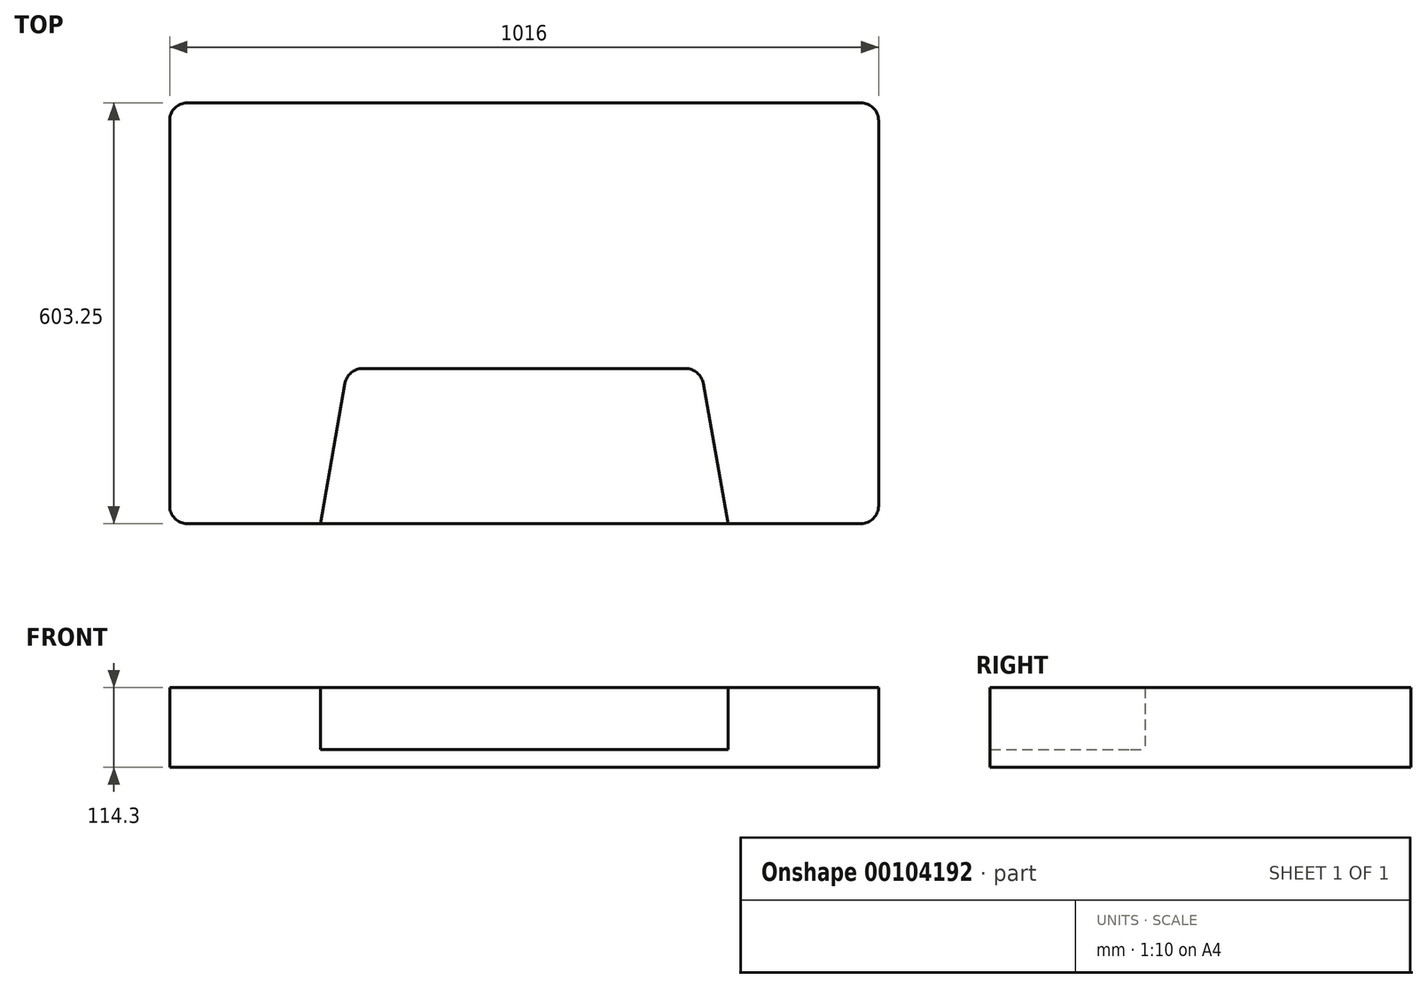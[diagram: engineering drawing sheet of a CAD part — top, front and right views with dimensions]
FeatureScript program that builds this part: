
annotation { "Feature Type Name" : "Feature", "Feature Type Description" : "" }
export const myFeature = defineFeature(function(context is Context, id is Id, definition is map)
    precondition{}
    {
        {
            var Q0;
            Q0=qCreatedBy(makeId("Top.planeOp"),FACE);
            var sketch = newSketch(context, id + "F0", { "sketchPlane" : qUnion([Q0])});
            skLineSegment(sketch, "E0.bottom", {"start": v(-508, 0) * mm, "end": v(508, 0) * mm});
            skLineSegment(sketch, "E0.top", {"start": v(-508, -603.25) * mm, "end": v(508, -603.25) * mm});
            skLineSegment(sketch, "E0.left", {"start": v(-508, 0) * mm, "end": v(-508, -603.25) * mm});
            skLineSegment(sketch, "E0.right", {"start": v(508, 0) * mm, "end": v(508, -603.25) * mm});
            skLineSegment(sketch, "E1", {"start": v(-292.1, -603.25) * mm, "end": v(-252.91, -381) * mm});
            skLineSegment(sketch, "E2", {"start": v(-252.91, -381) * mm, "end": v(252.91, -381) * mm});
            skLineSegment(sketch, "E3", {"start": v(252.91, -381) * mm, "end": v(292.1, -603.25) * mm});
            skLineSegment(sketch, "E4", {"start": v(0, 0) * mm, "end": v(0, -381) * mm, "construction": true});
            skSolve(sketch);
        }
        {
            var Q0;
            Q0=qSketchRegion(id+"F0",true);
            extrude(context, id + "F1", {"entities" : qUnion([Q0]), "depth" : 114.3 * mm});
        }
        {
            var Q0;
            {var subQ1=sQuery(id+"F0.wireOp",EDGE,"E1");Q0=makeQuery(id+"F0.imprint","IMPRINT",FACE,{"disambiguationData":[TD([[makeQuery(id+"F0.imprint","IMPRINT",EDGE,{"derivedFrom":subQ1}),-1.0]])]});}
            extrude(context, id + "F2", {"entities" : qUnion([Q0]), "operationType" : NewBodyOperationType.REMOVE, "endBound" : BoundingType.THROUGH_ALL, "depth" : 50.8 * mm, "hasSecondDirection" : true, "secondDirectionOppositeDirection" : false, "secondDirectionDepth" : 25.4 * mm});
        }
        {
            var Q0;
            Q0=makeQuery(id+"F1.opExtrude","SWEPT_EDGE",EDGE,{"disambiguationData":[OSD([sQuery(id+"F0.wireOp",EDGE,"E0.top"),sQuery(id+"F0.wireOp",EDGE,"E0.left")])]});
            var Q1;
            Q1=makeQuery(id+"F1.opExtrude","SWEPT_EDGE",EDGE,{"disambiguationData":[OSD([sQuery(id+"F0.wireOp",EDGE,"E0.top"),sQuery(id+"F0.wireOp",EDGE,"E0.right")])]});
            var Q2;
            Q2=makeQuery(id+"F2.boolean.opBoolean","COPY",EDGE,{"derivedFrom":makeQuery(id+"F2.opExtrude","SWEPT_EDGE",EDGE,{"disambiguationData":[OSD([sQuery(id+"F0.wireOp",EDGE,"E0.top"),sQuery(id+"F0.wireOp",EDGE,"E1")])]})});
            var Q3;
            Q3=makeQuery(id+"F2.boolean.opBoolean","COPY",EDGE,{"derivedFrom":makeQuery(id+"F2.opExtrude","SWEPT_EDGE",EDGE,{"disambiguationData":[OSD([sQuery(id+"F0.wireOp",EDGE,"E1"),sQuery(id+"F0.wireOp",EDGE,"E2")])]})});
            var Q4;
            Q4=makeQuery(id+"F2.boolean.opBoolean","COPY",EDGE,{"derivedFrom":makeQuery(id+"F2.opExtrude","SWEPT_EDGE",EDGE,{"disambiguationData":[OSD([sQuery(id+"F0.wireOp",EDGE,"E0.top"),sQuery(id+"F0.wireOp",EDGE,"E3")])]})});
            var Q5;
            Q5=makeQuery(id+"F1.opExtrude","SWEPT_EDGE",EDGE,{"disambiguationData":[OSD([sQuery(id+"F0.wireOp",EDGE,"E0.bottom"),sQuery(id+"F0.wireOp",EDGE,"E0.right")])]});
            var Q6;
            Q6=makeQuery(id+"F2.boolean.opBoolean","COPY",EDGE,{"derivedFrom":makeQuery(id+"F2.opExtrude","SWEPT_EDGE",EDGE,{"disambiguationData":[OSD([sQuery(id+"F0.wireOp",EDGE,"E2"),sQuery(id+"F0.wireOp",EDGE,"E3")])]})});
            var Q7;
            Q7=makeQuery(id+"F1.opExtrude","SWEPT_EDGE",EDGE,{"disambiguationData":[OSD([sQuery(id+"F0.wireOp",EDGE,"E0.bottom"),sQuery(id+"F0.wireOp",EDGE,"E0.left")])]});
            fillet(context, id + "F3", {"entities" : qUnion([Q0, Q1, Q2, Q3, Q4, Q5, Q6, Q7]), "radius" : 25.4 * mm, "tangentPropagation" : true, "allowEdgeOverflow" : false});
        }
    });
